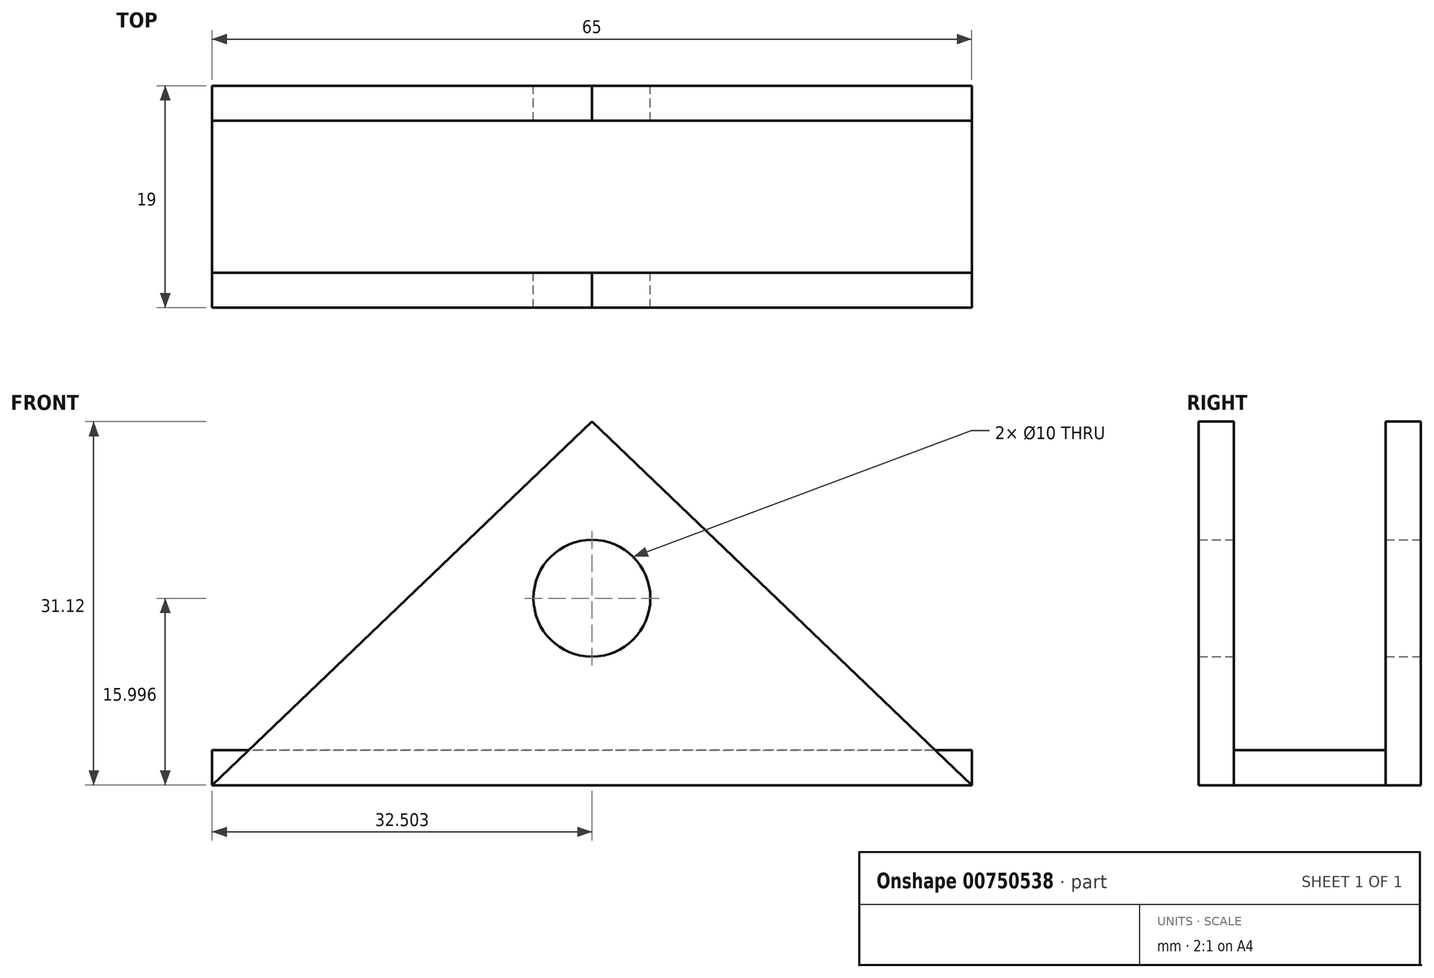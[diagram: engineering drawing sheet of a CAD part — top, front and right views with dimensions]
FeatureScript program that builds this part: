
annotation { "Feature Type Name" : "Feature", "Feature Type Description" : "" }
export const myFeature = defineFeature(function(context is Context, id is Id, definition is map)
    precondition{}
    {
        {
            var Q0;
            Q0=qCreatedBy(makeId("Front.planeOp"),FACE);
            cPlane(context, id + "F0", {"entities" : qUnion([Q0]), "cplaneType" : CPlaneType.OFFSET, "offset" : (9.5 - 3) * mm, "width" : 150 * mm, "height" : 150 * mm});
        }
        {
            var Q0;
            Q0=qCreatedBy(id+"F0.planeOp",FACE);
            var sketch = newSketch(context, id + "F1", { "sketchPlane" : qUnion([Q0])});
            skLineSegment(sketch, "E0", {"start": v(5.01, 3.8) * mm, "end": v(70.01, 3.8) * mm});
            skLineSegment(sketch, "E1", {"start": v(5.01, 3.8) * mm, "end": v(37.51, 34.93) * mm});
            skLineSegment(sketch, "E2", {"start": v(37.51, 34.93) * mm, "end": v(70.01, 3.8) * mm});
            skSolve(sketch);
        }
        {
            var Q0;
            Q0 = qSketchRegion(id + "F1", true);
            extrude(context, id + "F2", {"entities" : qUnion([Q0]), "depth" : 3 * mm, "offsetDistance" : 25 * mm});
        }
        {
            var Q0;
            Q0=makeQuery(id+"F2.opExtrude","SWEPT_BODY",BODY,{"disambiguationData":[OSD([sQuery(id+"F1.wireOp",EDGE,"E0"),sQuery(id+"F1.wireOp",EDGE,"E1"),sQuery(id+"F1.wireOp",EDGE,"E2")])]});
            var Q1;
            Q1=qCreatedBy(makeId("Front.planeOp"),FACE);
            mirror(context, id + "F3", {"entities" : qUnion([Q0]), "mirrorPlane" : qUnion([Q1])});
        }
        {
            var Q0;
            Q0=makeQuery(id+"F3.opPattern","COPY",FACE,{"derivedFrom":makeQuery(id+"F2.opExtrude","SWEPT_FACE",FACE,{"disambiguationData":[OSD([sQuery(id+"F1.wireOp",EDGE,"E0")])]}),"instanceName":"1"});
            var sketch = newSketch(context, id + "F4", { "sketchPlane" : qUnion([Q0])});
            skLineSegment(sketch, "E3.bottom", {"start": v(70.01, -6.5) * mm, "end": v(5.01, -6.5) * mm});
            skLineSegment(sketch, "E3.top", {"start": v(70.01, 6.5) * mm, "end": v(5.01, 6.5) * mm});
            skLineSegment(sketch, "E3.left", {"start": v(70.01, -6.5) * mm, "end": v(70.01, 6.5) * mm});
            skLineSegment(sketch, "E3.right", {"start": v(5.01, -6.5) * mm, "end": v(5.01, 6.5) * mm});
            skSolve(sketch);
        }
        {
            var Q0;
            Q0=makeQuery(id+"F4.imprint","IMPRINT",FACE,{"disambiguationData":[TD([[makeQuery(id+"F4.imprint","IMPRINT",EDGE,{"derivedFrom":sQuery(id+"F4.wireOp",EDGE,"E3.bottom")}),1.0]])]});
            extrude(context, id + "F5", {"entities" : qUnion([Q0]), "oppositeDirection" : true, "depth" : 3 * mm, "offsetDistance" : 25 * mm});
        }
        {
            var Q0;
            Q0=qCreatedBy(makeId("Front.planeOp"),FACE);
            var sketch = newSketch(context, id + "F6", { "sketchPlane" : qUnion([Q0])});
            skCircle(sketch, "E4", {"center": v(37.51, 19.8) * mm, "radius": 5 * mm});
            skSolve(sketch);
        }
        {
            var Q0;
            Q0=makeQuery(id+"F6.imprint","IMPRINT",FACE,{"disambiguationData":[TD([[makeQuery(id+"F6.imprint","IMPRINT",EDGE,{"derivedFrom":sQuery(id+"F6.wireOp",EDGE,"E4")}),1.0]])]});
            var Q1;
            Q1=sQuery(id+"F6.wireOp",EDGE,"E4");
            extrude(context, id + "F7", {"entities" : qUnion([Q0]), "operationType" : NewBodyOperationType.REMOVE, "surfaceEntities" : qUnion([Q1]), "endBound" : BoundingType.SYMMETRIC, "depth" : 25 * mm, "offsetDistance" : 25 * mm});
        }
    });
